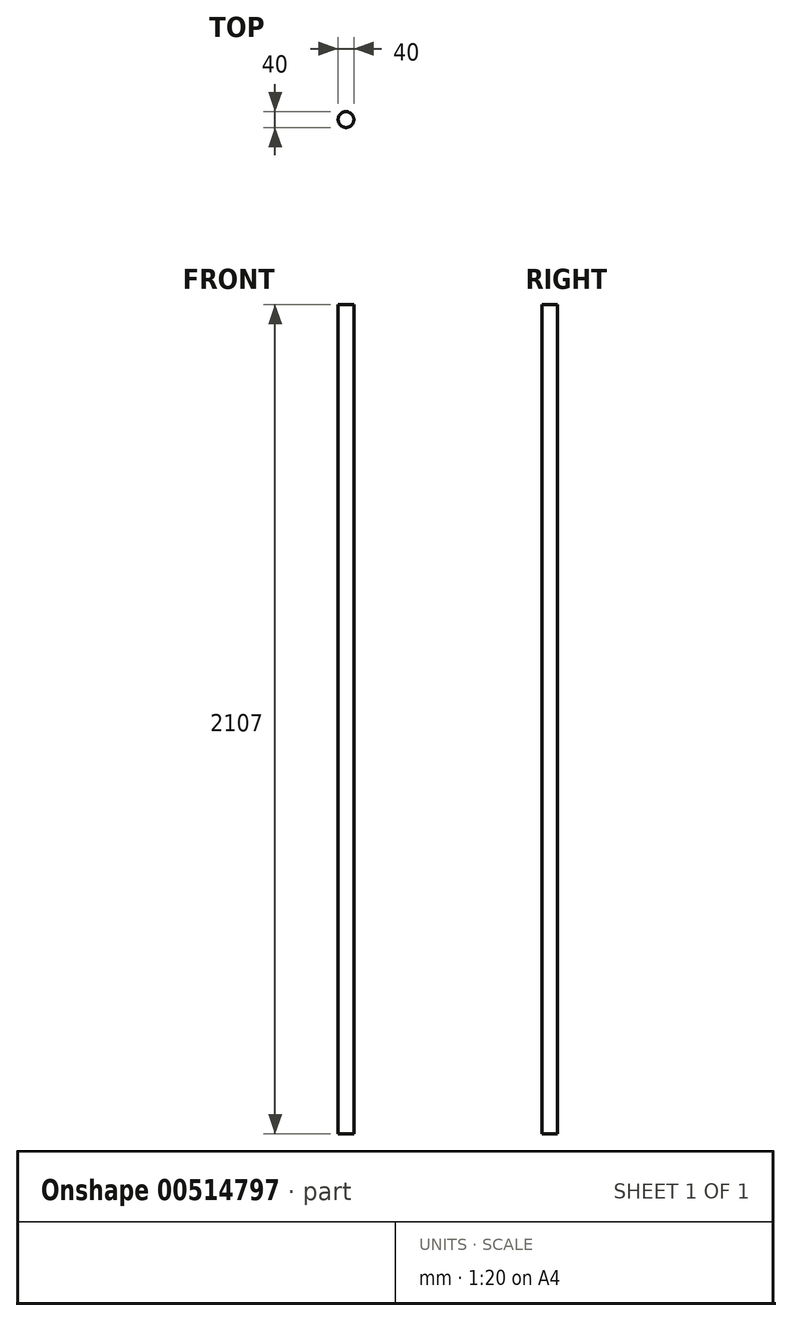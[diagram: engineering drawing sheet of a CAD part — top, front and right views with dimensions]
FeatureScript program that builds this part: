
annotation { "Feature Type Name" : "Feature", "Feature Type Description" : "" }
export const myFeature = defineFeature(function(context is Context, id is Id, definition is map)
    precondition{}
    {
        {
            var Q0;
            Q0=qCreatedBy(makeId("Top.planeOp"),FACE);
            var sketch = newSketch(context, id + "F0", { "sketchPlane" : qUnion([Q0])});
            skCircle(sketch, "E0", {"center": v(0, 0) * mm, "radius": 20 * mm});
            skLineSegment(sketch, "E1", {"start": v(20, 30.55) * mm, "end": v(20, -31.41) * mm, "construction": true});
            skSolve(sketch);
        }
        {
            var Q0;
            Q0=makeQuery(id+"F0.imprint","IMPRINT",FACE,{"disambiguationData":[TD([[makeQuery(id+"F0.imprint","IMPRINT",EDGE,{"derivedFrom":sQuery(id+"F0.wireOp",EDGE,"E0")}),1.0]])]});
            extrude(context, id + "F1", {"entities" : qUnion([Q0]), "depth" : 2000 * mm, "offsetDistance" : 25 * mm, "hasSecondDirection" : true, "secondDirectionOppositeDirection" : true, "secondDirectionDepth" : 107 * mm});
        }
    });
